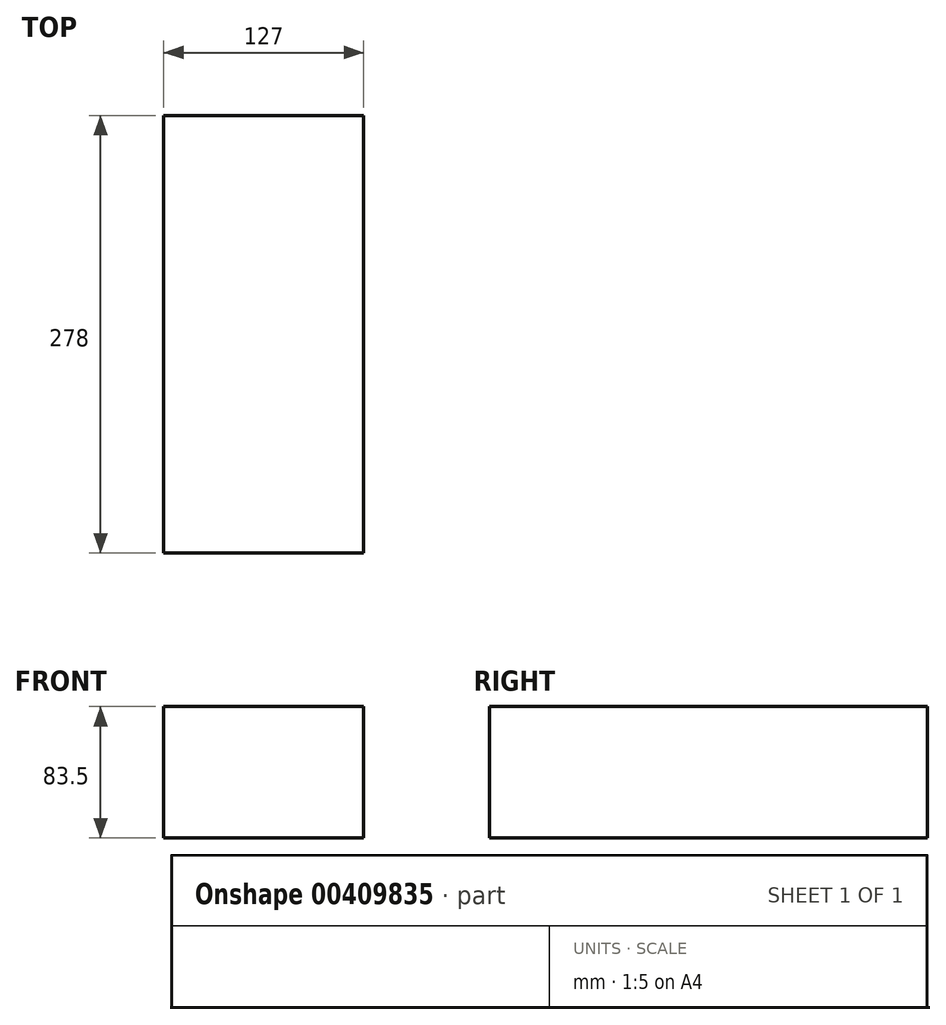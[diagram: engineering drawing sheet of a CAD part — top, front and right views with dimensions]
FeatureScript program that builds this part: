
annotation { "Feature Type Name" : "Feature", "Feature Type Description" : "" }
export const myFeature = defineFeature(function(context is Context, id is Id, definition is map)
    precondition{}
    {
        {
            var Q0;
            Q0=qCreatedBy(makeId("Front.planeOp"),FACE);
            var sketch = newSketch(context, id + "F0", { "sketchPlane" : qUnion([Q0])});
            skLineSegment(sketch, "E0.bottom", {"start": v(0, 0) * mm, "end": v(127, 0) * mm});
            skLineSegment(sketch, "E0.top", {"start": v(0, 83.5) * mm, "end": v(127, 83.5) * mm});
            skLineSegment(sketch, "E0.left", {"start": v(0, 0) * mm, "end": v(0, 83.5) * mm});
            skLineSegment(sketch, "E0.right", {"start": v(127, 0) * mm, "end": v(127, 83.5) * mm});
            skSolve(sketch);
        }
        {
            var Q0;
            Q0 = qSketchRegion(id + "F0", true);
            extrude(context, id + "F1", {"entities" : qUnion([Q0]), "depth" : 278 * mm});
        }
    });
